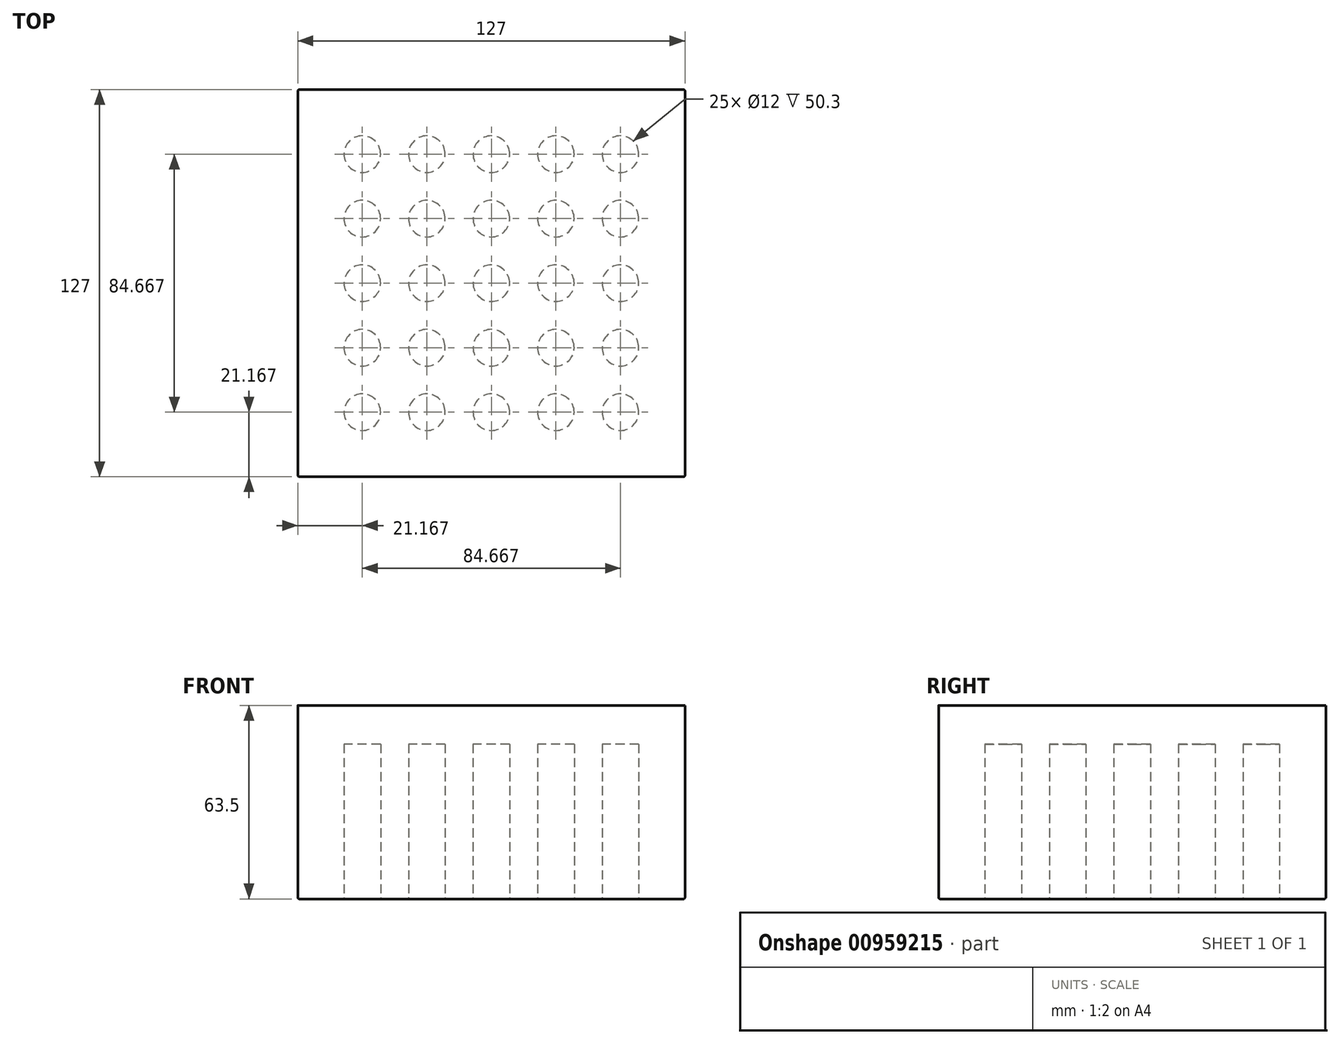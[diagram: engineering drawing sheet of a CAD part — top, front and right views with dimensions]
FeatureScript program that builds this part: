
annotation { "Feature Type Name" : "Feature", "Feature Type Description" : "" }
export const myFeature = defineFeature(function(context is Context, id is Id, definition is map)
    precondition{}
    {
        {
            var Q0;
            Q0=qCreatedBy(makeId("Top.planeOp"),FACE);
            var sketch = newSketch(context, id + "F0", { "sketchPlane" : qUnion([Q0])});
            skLineSegment(sketch, "E0.bottom", {"start": v(63.5, 63.5) * mm, "end": v(-63.5, 63.5) * mm});
            skLineSegment(sketch, "E0.top", {"start": v(63.5, -63.5) * mm, "end": v(-63.5, -63.5) * mm});
            skLineSegment(sketch, "E0.left", {"start": v(63.5, 63.5) * mm, "end": v(63.5, -63.5) * mm});
            skLineSegment(sketch, "E0.right", {"start": v(-63.5, 63.5) * mm, "end": v(-63.5, -63.5) * mm});
            skPoint(sketch, "E0.middle", {"position": v(0, 0) * mm});
            skSolve(sketch);
        }
        {
            var Q0;
            Q0=qSketchRegion(id+"F0",true);
            extrude(context, id + "F1", {"entities" : qUnion([Q0]), "depth" : 63.5 * mm, "offsetDistance" : 25.4 * mm});
        }
        {
            var Q0;
            Q0=makeQuery(id+"F1.opExtrude","CAP_FACE",FACE,{"disambiguationData":[OSD([sQuery(id+"F0.wireOp",EDGE,"E0.bottom"),sQuery(id+"F0.wireOp",EDGE,"E0.top"),sQuery(id+"F0.wireOp",EDGE,"E0.left"),sQuery(id+"F0.wireOp",EDGE,"E0.right")])],"isStart":false});
            var sketch = newSketch(context, id + "F2", { "sketchPlane" : qUnion([Q0])});
            skLineSegment(sketch, "E1.bottom", {"start": v(63.5, 63.5) * mm, "end": v(-63.5, 63.5) * mm});
            skLineSegment(sketch, "E1.top", {"start": v(63.5, -63.5) * mm, "end": v(-63.5, -63.5) * mm});
            skLineSegment(sketch, "E1.left", {"start": v(63.5, 63.5) * mm, "end": v(63.5, -63.5) * mm});
            skLineSegment(sketch, "E1.right", {"start": v(-63.5, 63.5) * mm, "end": v(-63.5, -63.5) * mm});
            skPoint(sketch, "E1.middle", {"position": v(0, 0) * mm});
            skSolve(sketch);
        }
        {
            var Q0;
            Q0=qCreatedBy(makeId("Top.planeOp"),FACE);
            var sketch = newSketch(context, id + "F3", { "sketchPlane" : qUnion([Q0])});
            skLineSegment(sketch, "E2", {"start": v(-63.5, 63.5) * mm, "end": v(-63.5, -63.5) * mm, "construction": true});
            skLineSegment(sketch, "E3.1.0.0", {"start": v(-42.33, 63.5) * mm, "end": v(-42.33, -63.5) * mm, "construction": true});
            skLineSegment(sketch, "E3.2.0.0", {"start": v(-21.17, 63.5) * mm, "end": v(-21.17, -63.5) * mm, "construction": true});
            skLineSegment(sketch, "E3.3.0.0", {"start": v(0, 63.5) * mm, "end": v(0, -63.5) * mm, "construction": true});
            skLineSegment(sketch, "E3.4.0.0", {"start": v(21.17, 63.5) * mm, "end": v(21.17, -63.5) * mm, "construction": true});
            skLineSegment(sketch, "E3.5.0.0", {"start": v(42.33, 63.5) * mm, "end": v(42.33, -63.5) * mm, "construction": true});
            skLineSegment(sketch, "E3.direction1", {"start": v(-63.5, -63.5) * mm, "end": v(-42.33, -63.5) * mm, "construction": true});
            skLineSegment(sketch, "E4", {"start": v(-63.5, -63.5) * mm, "end": v(63.5, -63.5) * mm, "construction": true});
            skLineSegment(sketch, "E5.0.1.0", {"start": v(-63.5, -42.33) * mm, "end": v(63.5, -42.33) * mm, "construction": true});
            skLineSegment(sketch, "E5.0.2.0", {"start": v(-63.5, -21.17) * mm, "end": v(63.5, -21.17) * mm, "construction": true});
            skLineSegment(sketch, "E5.0.3.0", {"start": v(-63.5, 0) * mm, "end": v(63.5, 0) * mm, "construction": true});
            skLineSegment(sketch, "E5.0.4.0", {"start": v(-63.5, 21.17) * mm, "end": v(63.5, 21.17) * mm, "construction": true});
            skLineSegment(sketch, "E5.0.5.0", {"start": v(-63.5, 42.33) * mm, "end": v(63.5, 42.33) * mm, "construction": true});
            skLineSegment(sketch, "E5.direction1", {"start": v(-63.5, -63.5) * mm, "end": v(-38.5, -63.5) * mm, "construction": true});
            skLineSegment(sketch, "E5.direction2", {"start": v(-63.5, -63.5) * mm, "end": v(-63.5, -42.33) * mm, "construction": true});
            skCircle(sketch, "E6", {"center": v(-42.33, -42.33) * mm, "radius": 6 * mm});
            skCircle(sketch, "E7.0.1.0", {"center": v(-42.33, -21.17) * mm, "radius": 6 * mm});
            skCircle(sketch, "E7.0.2.0", {"center": v(-42.33, 0) * mm, "radius": 6 * mm});
            skCircle(sketch, "E7.0.3.0", {"center": v(-42.33, 21.17) * mm, "radius": 6 * mm});
            skCircle(sketch, "E7.0.4.0", {"center": v(-42.33, 42.33) * mm, "radius": 6 * mm});
            skCircle(sketch, "E7.1.0.0", {"center": v(-21.17, -42.33) * mm, "radius": 6 * mm});
            skCircle(sketch, "E7.1.1.0", {"center": v(-21.17, -21.17) * mm, "radius": 6 * mm});
            skCircle(sketch, "E7.1.2.0", {"center": v(-21.17, 0) * mm, "radius": 6 * mm});
            skCircle(sketch, "E7.1.3.0", {"center": v(-21.17, 21.17) * mm, "radius": 6 * mm});
            skCircle(sketch, "E7.1.4.0", {"center": v(-21.17, 42.33) * mm, "radius": 6 * mm});
            skCircle(sketch, "E7.2.0.0", {"center": v(0, -42.33) * mm, "radius": 6 * mm});
            skCircle(sketch, "E7.2.1.0", {"center": v(0, -21.17) * mm, "radius": 6 * mm});
            skCircle(sketch, "E7.2.2.0", {"center": v(0, 0) * mm, "radius": 6 * mm});
            skCircle(sketch, "E7.2.3.0", {"center": v(0, 21.17) * mm, "radius": 6 * mm});
            skCircle(sketch, "E7.2.4.0", {"center": v(0, 42.33) * mm, "radius": 6 * mm});
            skCircle(sketch, "E7.3.0.0", {"center": v(21.17, -42.33) * mm, "radius": 6 * mm});
            skCircle(sketch, "E7.3.1.0", {"center": v(21.17, -21.17) * mm, "radius": 6 * mm});
            skCircle(sketch, "E7.3.2.0", {"center": v(21.17, 0) * mm, "radius": 6 * mm});
            skCircle(sketch, "E7.3.3.0", {"center": v(21.17, 21.17) * mm, "radius": 6 * mm});
            skCircle(sketch, "E7.3.4.0", {"center": v(21.17, 42.33) * mm, "radius": 6 * mm});
            skCircle(sketch, "E7.4.0.0", {"center": v(42.33, -42.33) * mm, "radius": 6 * mm});
            skCircle(sketch, "E7.4.1.0", {"center": v(42.33, -21.17) * mm, "radius": 6 * mm});
            skCircle(sketch, "E7.4.2.0", {"center": v(42.33, 0) * mm, "radius": 6 * mm});
            skCircle(sketch, "E7.4.3.0", {"center": v(42.33, 21.17) * mm, "radius": 6 * mm});
            skCircle(sketch, "E7.4.4.0", {"center": v(42.33, 42.33) * mm, "radius": 6 * mm});
            skLineSegment(sketch, "E7.direction1", {"start": v(-42.33, -42.33) * mm, "end": v(-21.17, -42.33) * mm, "construction": true});
            skLineSegment(sketch, "E7.direction2", {"start": v(-42.33, -42.33) * mm, "end": v(-42.33, -21.17) * mm, "construction": true});
            skSolve(sketch);
        }
        {
            var Q0;
            Q0=qSketchRegion(id+"F3",true);
            extrude(context, id + "F4", {"entities" : qUnion([Q0]), "operationType" : NewBodyOperationType.REMOVE, "depth" : 50.8 * mm, "offsetDistance" : 25 * mm});
        }
        {
            var Q0;
            Q0=makeQuery(id+"F1.opExtrude","CAP_FACE",FACE,{"disambiguationData":[OSD([sQuery(id+"F0.wireOp",EDGE,"E0.bottom"),sQuery(id+"F0.wireOp",EDGE,"E0.top"),sQuery(id+"F0.wireOp",EDGE,"E0.left"),sQuery(id+"F0.wireOp",EDGE,"E0.right")])],"isStart":true});
            var Q1;
            Q1=makeQuery(id+"F1.opExtrude","SWEPT_EDGE",EDGE,{"disambiguationData":[OSD([sQuery(id+"F0.wireOp",EDGE,"E0.bottom"),sQuery(id+"F0.wireOp",EDGE,"E0.right")])]});
            var Q2;
            Q2=makeQuery(id+"F1.opExtrude","SWEPT_EDGE",EDGE,{"disambiguationData":[OSD([sQuery(id+"F0.wireOp",EDGE,"E0.top"),sQuery(id+"F0.wireOp",EDGE,"E0.right")])]});
            var Q3;
            Q3=makeQuery(id+"F1.opExtrude","SWEPT_EDGE",EDGE,{"disambiguationData":[OSD([sQuery(id+"F0.wireOp",EDGE,"E0.bottom"),sQuery(id+"F0.wireOp",EDGE,"E0.left")])]});
            var Q4;
            Q4=makeQuery(id+"F1.opExtrude","SWEPT_EDGE",EDGE,{"disambiguationData":[OSD([sQuery(id+"F0.wireOp",EDGE,"E0.top"),sQuery(id+"F0.wireOp",EDGE,"E0.left")])]});
            fillet(context, id + "F5", {"entities" : qUnion([Q0, Q1, Q2, Q3, Q4]), "radius" : 0.5 * mm, "tangentPropagation" : true, "allowEdgeOverflow" : false});
        }
    });
